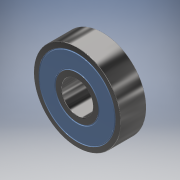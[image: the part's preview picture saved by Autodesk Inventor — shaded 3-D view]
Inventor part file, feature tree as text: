
AUTODESK INVENTOR PART (.ipt)
format: ipt  version: 2017.1 (Build 211199000, 199)  size: 198,656 bytes
history: native  units: in
note: dims shown in document units (in); Inventor stores cm internally (conversion verified against a paired STEP export)
features: sketch x2, extrude x1, fillet x1, revolve x1, plane x1, mirror x1
ambient origin geometry x8: Origin, YZ Plane, XZ Plane, XY Plane, X Axis, Y Axis, Z Axis, Center Point
bodies: Solid1 (feature_tree)
feature tree (7):
  extrude  "Extrusion1"  Depth=0.5512in
  fillet  "Fillet1"  Radius=0.5512in
  revolve  "Revolution1"  Angle=90.0deg
  plane  "Work Plane1"
  mirror  "Mirror1"
  sketch  "Sketch1"  dims[d0=0.6693in d1=1.8504in d2=0.5512in d3=0.0in]
  sketch  "Sketch2"  dims[d4=0.0118in d5=90.0deg]
